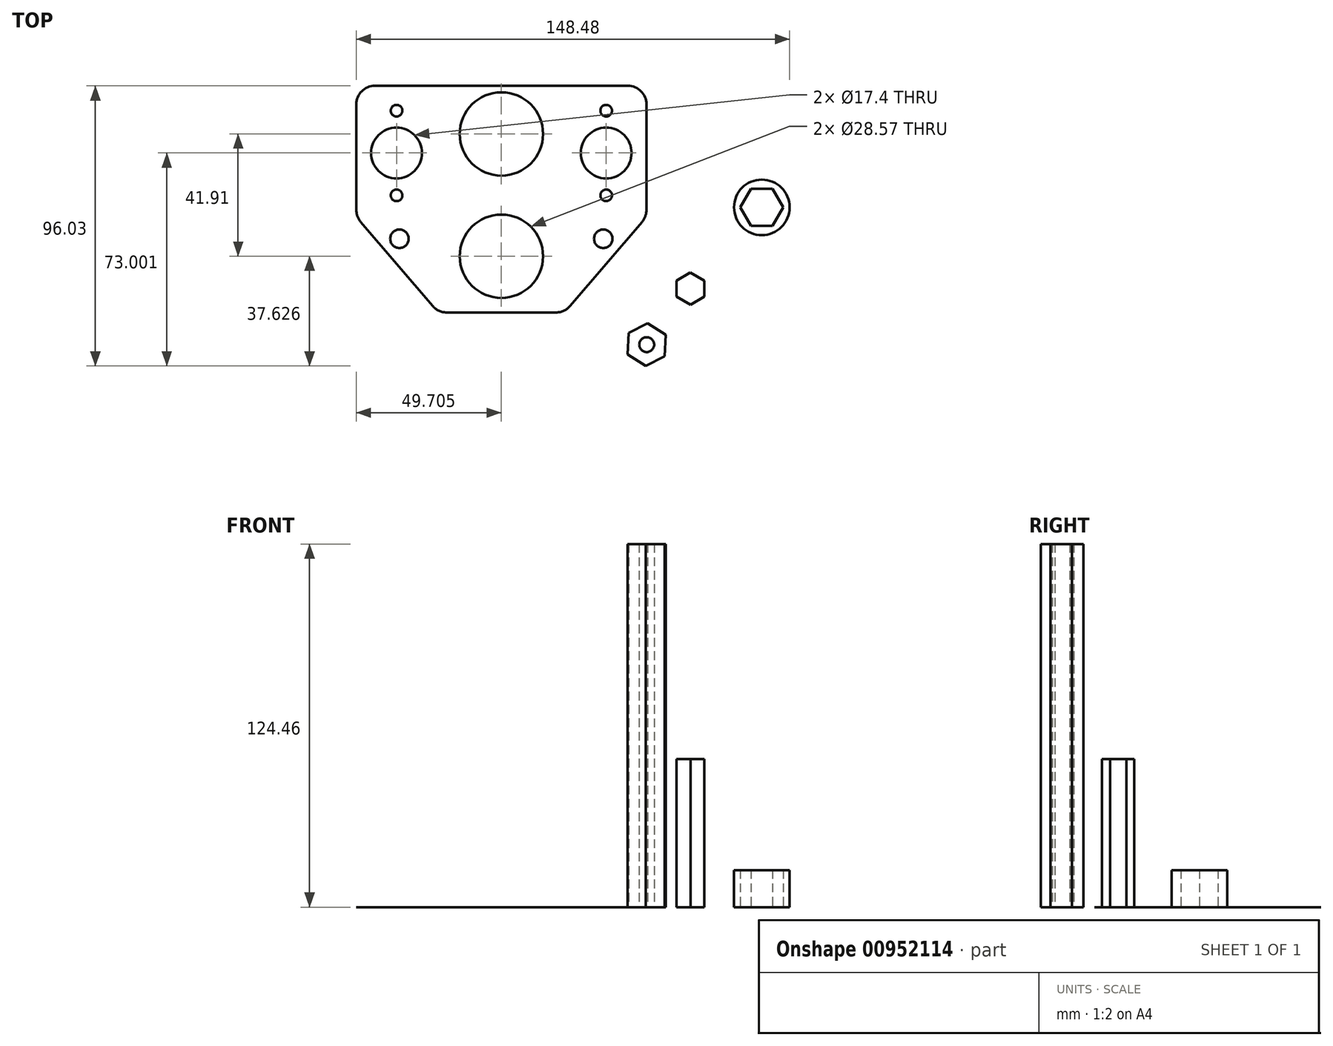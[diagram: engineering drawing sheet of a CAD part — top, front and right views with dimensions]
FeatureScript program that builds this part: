
annotation { "Feature Type Name" : "Feature", "Feature Type Description" : "" }
export const myFeature = defineFeature(function(context is Context, id is Id, definition is map)
    precondition{}
    {
        {
            var Q0;
            Q0=qCreatedBy(makeId("Top.planeOp"),FACE);
            var sketch = newSketch(context, id + "F0", { "sketchPlane" : qUnion([Q0])});
            skCircle(sketch, "E0", {"center": v(-88.96, 20.7) * mm, "radius": 8.7 * mm});
            skCircle(sketch, "E1", {"center": v(-17.11, 20.7) * mm, "radius": 8.7 * mm});
            skCircle(sketch, "E2", {"center": v(-88.96, 20.7) * mm, "radius": 4.76 * mm, "construction": true});
            skCircle(sketch, "E3", {"center": v(-17.11, 20.7) * mm, "radius": 4.76 * mm, "construction": true});
            skCircle(sketch, "E4", {"center": v(-53.04, 27.24) * mm, "radius": 31.75 * mm, "construction": true});
            skCircle(sketch, "E5", {"center": v(-53.04, 27.24) * mm, "radius": 14.29 * mm});
            skCircle(sketch, "E6", {"center": v(-53.04, -14.67) * mm, "radius": 14.29 * mm});
            skCircle(sketch, "E7", {"center": v(-53.04, 27.24) * mm, "radius": 13.97 * mm, "construction": true});
            skCircle(sketch, "E8", {"center": v(-53.04, -14.67) * mm, "radius": 27.94 * mm, "construction": true});
            skLineSegment(sketch, "E9.bottom", {"start": v(-129.24, 10.73) * mm, "end": v(23.16, 10.73) * mm, "construction": true});
            skLineSegment(sketch, "E9.top", {"start": v(-129.24, -40.07) * mm, "end": v(23.16, -40.07) * mm, "construction": true});
            skLineSegment(sketch, "E9.left", {"start": v(-129.24, 10.73) * mm, "end": v(-129.24, -40.07) * mm, "construction": true});
            skLineSegment(sketch, "E9.right", {"start": v(23.16, 10.73) * mm, "end": v(23.16, -40.07) * mm, "construction": true});
            skLineSegment(sketch, "E10", {"start": v(-88.96, 35.2) * mm, "end": v(-88.96, 6.2) * mm, "construction": true});
            skLineSegment(sketch, "E11", {"start": v(-17.11, 35.2) * mm, "end": v(-17.11, 6.2) * mm, "construction": true});
            skCircle(sketch, "E12", {"center": v(-88.96, 35.2) * mm, "radius": 2 * mm});
            skCircle(sketch, "E13", {"center": v(-88.96, 6.2) * mm, "radius": 2 * mm});
            skCircle(sketch, "E14", {"center": v(-17.11, 35.2) * mm, "radius": 2 * mm});
            skCircle(sketch, "E15", {"center": v(-17.11, 6.2) * mm, "radius": 2 * mm});
            skLineSegment(sketch, "E16", {"start": v(-102.74, 43.73) * mm, "end": v(-102.74, -1.15) * mm});
            skLineSegment(sketch, "E17", {"start": v(-102.74, -1.15) * mm, "end": v(-74.72, -33.94) * mm});
            skLineSegment(sketch, "E18", {"start": v(-74.72, -33.94) * mm, "end": v(-31.35, -33.94) * mm});
            skLineSegment(sketch, "E19", {"start": v(-31.35, -33.94) * mm, "end": v(-3.33, -1.15) * mm});
            skLineSegment(sketch, "E20", {"start": v(-3.33, -1.15) * mm, "end": v(-3.33, 43.73) * mm});
            skLineSegment(sketch, "E21", {"start": v(-3.33, 43.73) * mm, "end": v(-102.74, 43.73) * mm});
            skPoint(sketch, "E22", {"position": v(-53.04, -33.94) * mm});
            skLineSegment(sketch, "E23", {"start": v(-87.96, -8.69) * mm, "end": v(-18.11, -8.69) * mm, "construction": true});
            skCircle(sketch, "E24", {"center": v(-18.11, -8.69) * mm, "radius": 3.18 * mm});
            skCircle(sketch, "E25", {"center": v(-87.96, -8.69) * mm, "radius": 3.18 * mm});
            skPoint(sketch, "E26", {"position": v(-53.04, -8.69) * mm});
            skCircle(sketch, "E27", {"center": v(-53.04, -14.67) * mm, "radius": 6.87 * mm});
            skSolve(sketch);
        }
        {
            var Q0;
            Q0=makeQuery(id+"F0.imprint","IMPRINT",FACE,{"disambiguationData":[TD([[makeQuery(id+"F0.imprint","IMPRINT",EDGE,{"derivedFrom":sQuery(id+"F0.wireOp",EDGE,"E0")}),-1.0]])]});
            extrude(context, id + "F1", {"entities" : qUnion([Q0]), "depth" : 1 / 101.6 * mm, "offsetDistance" : 25.4 * mm});
        }
        {
            var Q0;
            Q0=makeQuery(id+"F1.opExtrude","SWEPT_EDGE",EDGE,{"disambiguationData":[OSD([sQuery(id+"F0.wireOp",EDGE,"E16"),sQuery(id+"F0.wireOp",EDGE,"E21")])]});
            var Q1;
            Q1=makeQuery(id+"F1.opExtrude","SWEPT_EDGE",EDGE,{"disambiguationData":[OSD([sQuery(id+"F0.wireOp",EDGE,"E16"),sQuery(id+"F0.wireOp",EDGE,"E17")])]});
            var Q2;
            Q2=makeQuery(id+"F1.opExtrude","SWEPT_EDGE",EDGE,{"disambiguationData":[OSD([sQuery(id+"F0.wireOp",EDGE,"E17"),sQuery(id+"F0.wireOp",EDGE,"E18")])]});
            var Q3;
            Q3=makeQuery(id+"F1.opExtrude","SWEPT_EDGE",EDGE,{"disambiguationData":[OSD([sQuery(id+"F0.wireOp",EDGE,"E18"),sQuery(id+"F0.wireOp",EDGE,"E19")])]});
            var Q4;
            Q4=makeQuery(id+"F1.opExtrude","SWEPT_EDGE",EDGE,{"disambiguationData":[OSD([sQuery(id+"F0.wireOp",EDGE,"E19"),sQuery(id+"F0.wireOp",EDGE,"E20")])]});
            var Q5;
            Q5=makeQuery(id+"F1.opExtrude","SWEPT_EDGE",EDGE,{"disambiguationData":[OSD([sQuery(id+"F0.wireOp",EDGE,"E20"),sQuery(id+"F0.wireOp",EDGE,"E21")])]});
            fillet(context, id + "F2", {"entities" : qUnion([Q0, Q1, Q2, Q3, Q4, Q5]), "radius" : 6.35 * mm, "tangentPropagation" : true, "allowEdgeOverflow" : false});
        }
        {
            var Q0;
            Q0=qCreatedBy(makeId("Top.planeOp"),FACE);
            var sketch = newSketch(context, id + "F3", { "sketchPlane" : qUnion([Q0])});
            skCircle(sketch, "E28.cCircle", {"center": v(11.73, -25.79) * mm, "radius": 4.76 * mm, "construction": true});
            skLineSegment(sketch, "E28.0", {"start": v(16.5, -28.52) * mm, "end": v(11.76, -31.29) * mm});
            skLineSegment(sketch, "E28.1", {"start": v(11.76, -31.29) * mm, "end": v(6.98, -28.56) * mm});
            skLineSegment(sketch, "E28.2", {"start": v(6.98, -28.56) * mm, "end": v(6.96, -23.06) * mm});
            skLineSegment(sketch, "E28.3", {"start": v(6.96, -23.06) * mm, "end": v(11.7, -20.29) * mm});
            skLineSegment(sketch, "E28.4", {"start": v(11.7, -20.29) * mm, "end": v(16.48, -23.02) * mm});
            skLineSegment(sketch, "E28.5", {"start": v(16.48, -23.02) * mm, "end": v(16.5, -28.52) * mm});
            skPoint(sketch, "E28.0.midPoint", {"position": v(14.13, -29.9) * mm});
            skSolve(sketch);
        }
        {
            var Q0;
            Q0=makeQuery(id+"F3.imprint","IMPRINT",FACE,{"disambiguationData":[TD([[makeQuery(id+"F3.imprint","IMPRINT",EDGE,{"derivedFrom":sQuery(id+"F3.wireOp",EDGE,"E28.0")}),-1.0]])]});
            extrude(context, id + "F4", {"entities" : qUnion([Q0]), "depth" : 50.8 * mm, "offsetDistance" : 25.4 * mm});
        }
        {
            var Q0;
            Q0=qCreatedBy(makeId("Top.planeOp"),FACE);
            var sketch = newSketch(context, id + "F5", { "sketchPlane" : qUnion([Q0])});
            skCircle(sketch, "E29", {"center": v(-3.24, -44.97) * mm, "radius": 2.55 * mm});
            skCircle(sketch, "E30.cCircle", {"center": v(-3.24, -44.97) * mm, "radius": 6.35 * mm, "construction": true});
            skLineSegment(sketch, "E30.0", {"start": v(2.92, -48.95) * mm, "end": v(-3.6, -52.3) * mm});
            skLineSegment(sketch, "E30.1", {"start": v(-3.6, -52.3) * mm, "end": v(-9.76, -48.32) * mm});
            skLineSegment(sketch, "E30.2", {"start": v(-9.76, -48.32) * mm, "end": v(-9.4, -41) * mm});
            skLineSegment(sketch, "E30.3", {"start": v(-9.4, -41) * mm, "end": v(-2.87, -37.65) * mm});
            skLineSegment(sketch, "E30.4", {"start": v(-2.87, -37.65) * mm, "end": v(3.29, -41.63) * mm});
            skLineSegment(sketch, "E30.5", {"start": v(3.29, -41.63) * mm, "end": v(2.92, -48.95) * mm});
            skPoint(sketch, "E30.0.midPoint", {"position": v(-0.34, -50.62) * mm});
            skSolve(sketch);
        }
        {
            var Q0;
            Q0=makeQuery(id+"F5.imprint","IMPRINT",FACE,{"disambiguationData":[TD([[makeQuery(id+"F5.imprint","IMPRINT",EDGE,{"derivedFrom":sQuery(id+"F5.wireOp",EDGE,"E29")}),-1.0]])]});
            extrude(context, id + "F6", {"entities" : qUnion([Q0]), "depth" : 124.46 * mm, "offsetDistance" : 25.4 * mm});
        }
        {
            var Q0;
            Q0=qCreatedBy(makeId("Top.planeOp"),FACE);
            var sketch = newSketch(context, id + "F7", { "sketchPlane" : qUnion([Q0])});
            skCircle(sketch, "E31", {"center": v(36.21, 2.07) * mm, "radius": 9.53 * mm});
            skCircle(sketch, "E32.cCircle", {"center": v(36.21, 2.07) * mm, "radius": 6.35 * mm, "construction": true});
            skLineSegment(sketch, "E32.0", {"start": v(39.88, -4.28) * mm, "end": v(32.55, -4.28) * mm});
            skLineSegment(sketch, "E32.1", {"start": v(32.55, -4.28) * mm, "end": v(28.88, 2.07) * mm});
            skLineSegment(sketch, "E32.2", {"start": v(28.88, 2.07) * mm, "end": v(32.55, 8.42) * mm});
            skLineSegment(sketch, "E32.3", {"start": v(32.55, 8.42) * mm, "end": v(39.88, 8.42) * mm});
            skLineSegment(sketch, "E32.4", {"start": v(39.88, 8.42) * mm, "end": v(43.55, 2.07) * mm});
            skLineSegment(sketch, "E32.5", {"start": v(43.55, 2.07) * mm, "end": v(39.88, -4.28) * mm});
            skPoint(sketch, "E32.0.midPoint", {"position": v(36.21, -4.28) * mm});
            skSolve(sketch);
        }
        {
            var Q0;
            Q0=makeQuery(id+"F7.imprint","IMPRINT",FACE,{"disambiguationData":[TD([[makeQuery(id+"F7.imprint","IMPRINT",EDGE,{"derivedFrom":sQuery(id+"F7.wireOp",EDGE,"E31")}),1.0]])]});
            extrude(context, id + "F8", {"entities" : qUnion([Q0]), "depth" : 12.7 * mm, "offsetDistance" : 25.4 * mm});
        }
    });
